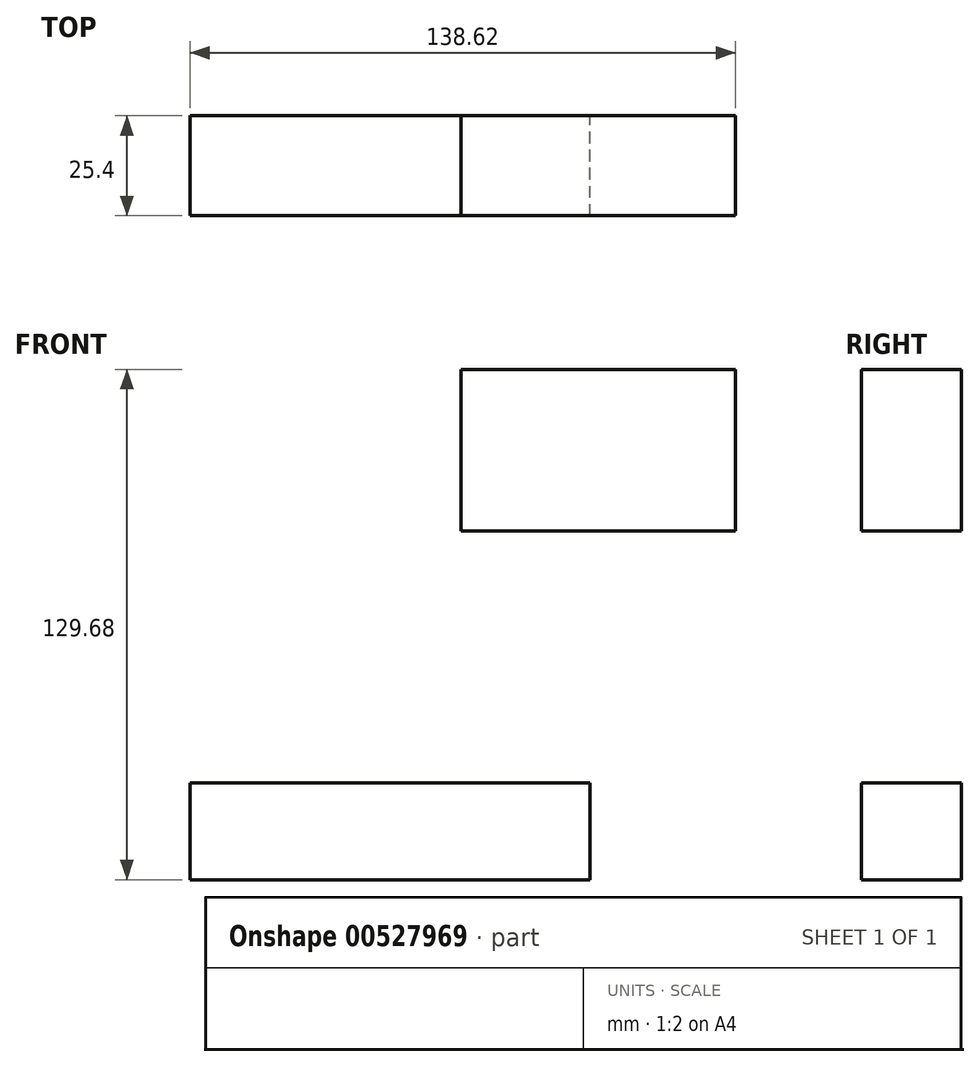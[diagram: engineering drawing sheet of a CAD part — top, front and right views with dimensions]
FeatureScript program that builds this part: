
annotation { "Feature Type Name" : "Feature", "Feature Type Description" : "" }
export const myFeature = defineFeature(function(context is Context, id is Id, definition is map)
    precondition{}
    {
        {
            var Q0;
            Q0=qCreatedBy(makeId("Front.planeOp"),FACE);
            var sketch = newSketch(context, id + "F0", { "sketchPlane" : qUnion([Q0])});
            skLineSegment(sketch, "E0.bottom", {"start": v(-50.8, 12.31) * mm, "end": v(50.8, 12.31) * mm});
            skLineSegment(sketch, "E0.top", {"start": v(-50.8, -12.31) * mm, "end": v(50.8, -12.31) * mm});
            skLineSegment(sketch, "E0.left", {"start": v(-50.8, 12.31) * mm, "end": v(-50.8, -12.31) * mm});
            skLineSegment(sketch, "E0.right", {"start": v(50.8, 12.31) * mm, "end": v(50.8, -12.31) * mm});
            skPoint(sketch, "E0.middle", {"position": v(0, 0) * mm});
            skLineSegment(sketch, "E1.bottom", {"start": v(87.82, 76.33) * mm, "end": v(18.06, 76.33) * mm});
            skLineSegment(sketch, "E1.top", {"start": v(87.82, 117.37) * mm, "end": v(18.06, 117.37) * mm});
            skLineSegment(sketch, "E1.left", {"start": v(87.82, 76.33) * mm, "end": v(87.82, 117.37) * mm});
            skLineSegment(sketch, "E1.right", {"start": v(18.06, 76.33) * mm, "end": v(18.06, 117.37) * mm});
            skPoint(sketch, "E1.middle", {"position": v(52.94, 96.85) * mm});
            skLineSegment(sketch, "E2", {"start": v(50.8, 12.31) * mm, "end": v(50.8, 38.58) * mm});
            skArc(sketch, "E3", {"start": v(50.8, 38.58) * mm, "mid": v(56.43, 52.36) * mm, "end": v(70.09, 58.28) * mm});
            skLineSegment(sketch, "E4", {"start": v(70.09, 58.28) * mm, "end": v(118.4, 58.28) * mm});
            skSolve(sketch);
        }
        {
            var Q0;
            Q0=makeQuery(id+"F0.imprint","IMPRINT",FACE,{"disambiguationData":[TD([[makeQuery(id+"F0.imprint","IMPRINT",EDGE,{"derivedFrom":sQuery(id+"F0.wireOp",EDGE,"E1.bottom")}),-1.0]])]});
            var Q1;
            Q1=makeQuery(id+"F0.imprint","IMPRINT",FACE,{"disambiguationData":[TD([[makeQuery(id+"F0.imprint","IMPRINT",EDGE,{"derivedFrom":sQuery(id+"F0.wireOp",EDGE,"E0.bottom")}),-1.0]])]});
            extrude(context, id + "F1", {"entities" : qUnion([Q0, Q1]), "depth" : 25.4 * mm, "offsetDistance" : 25.4 * mm});
        }
    });
